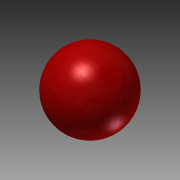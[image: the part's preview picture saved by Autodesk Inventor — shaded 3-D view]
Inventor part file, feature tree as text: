
AUTODESK INVENTOR PART (.ipt)
format: ipt  version: 2014 (Build 180170000, 170)  size: 135,680 bytes
history: native  units: in
note: dims shown in document units (in); Inventor stores cm internally (conversion verified against a paired STEP export)
features: revolve x1, sketch x1
ambient origin geometry x8: Origin, YZ Plane, XZ Plane, XY Plane, X Axis, Y Axis, Z Axis, Center Point
bodies: Solid1 (feature_tree)
feature tree (2):
  revolve  "Revolution1"  [1 undecoded]
  sketch  "Sketch1"  dims[d0=25.0in d1=0.125in d2=90.0deg]
note: 1 required parameter value undecoded (feature->parameter linkage not recoverable at this tier; creation-order binding heuristic only, values carry confidence <= 0.55)
